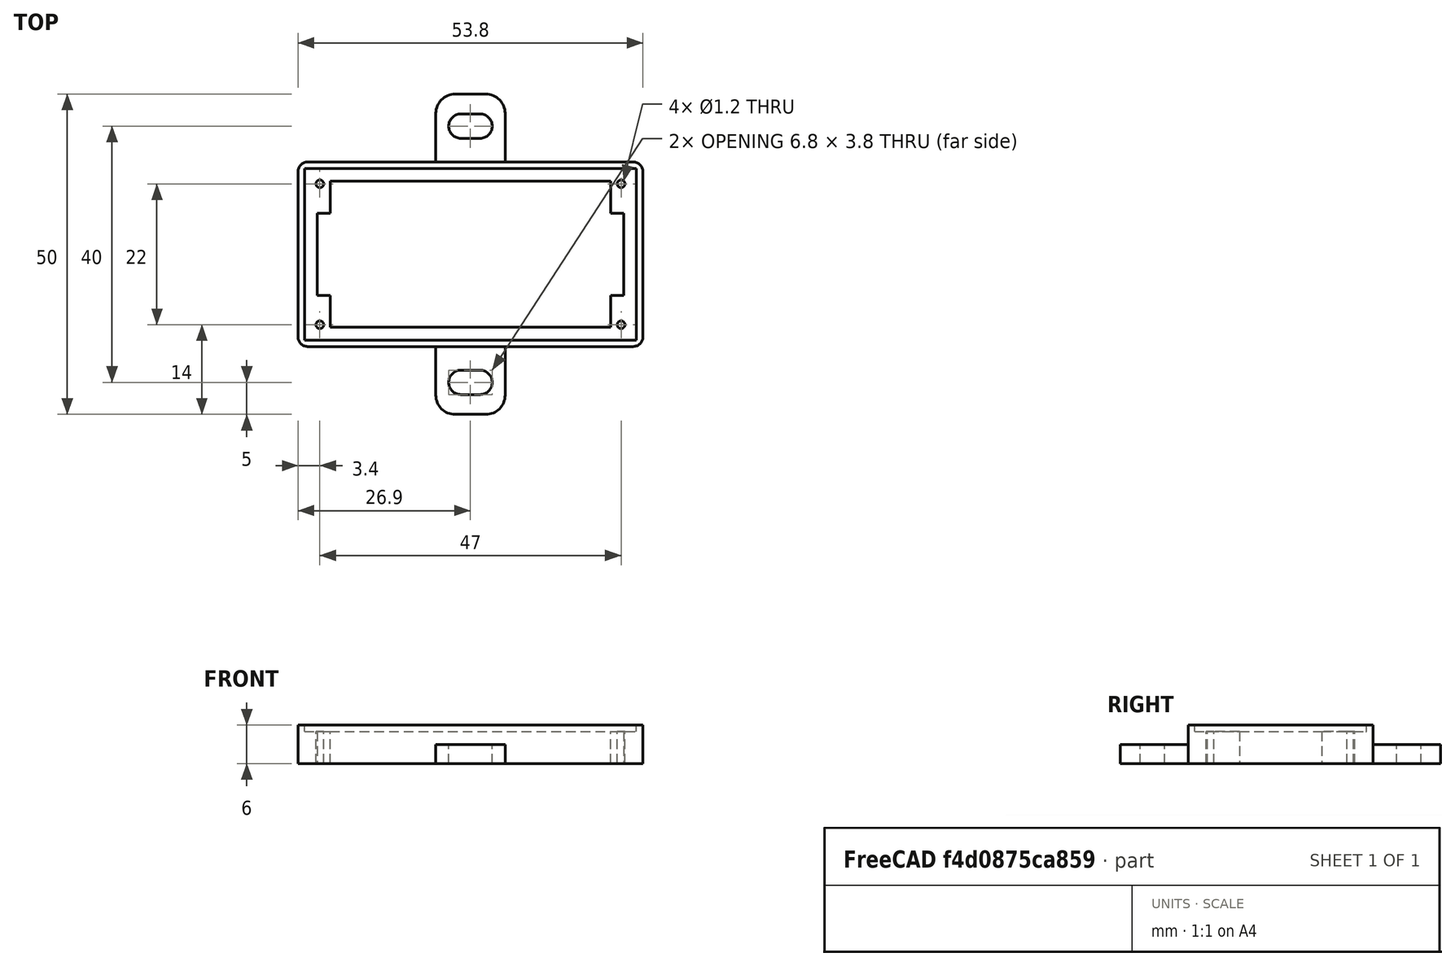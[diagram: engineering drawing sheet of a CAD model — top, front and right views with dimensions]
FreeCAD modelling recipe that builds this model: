
FCSTD DOCUMENT  (FreeCAD 0.18.4R)
Label: step_down_xl4015e1
License: All rights reserved
LicenseURL: http://en.wikipedia.org/wiki/All_rights_reserved
objects: Part::Box×4, Part::MultiFuse×3, Part::FeaturePython×2, Part::Cut×2, Spreadsheet::Sheet×1, Part::Cylinder×1, Part::Fillet×1, Part::Feature×1, App::Part×1
note: 14 computed .brp shape members not serialized (recipe doc carries the construction recipe); baked Part::Feature solids carry a one-line shape summary decoded from their .brp

FEATURE [Spreadsheet::Sheet] Spreadsheet  label="p"
  cells = A1=hole_x_dist; B1(hole_x_dist)=47; A2=hole_y_dist; B2(hole_y_dist)=22; A3=pcb_under; B3(pcb_under)=1.5; A4=pcb_x; B4(pcb_x)=51.8; A5=pcb_y; B5(pcb_y)=26.8; A6=hole_stand_x; B6(hole_stand_x)=4; A7=hole_stand_y; B7(hole_stand_y)=7; A8=hole_r; B8(hole_r)=0.6; A9=box_wall; B9(box_wall)=1; A10=under_layer; B10(under_layer)=3; A11=pcb_height; B11(pcb_height)=1.5
FEATURE [Part::Box] Box  label="bottom cube"
  AttacherType = Attacher::AttachEngine3D
  Height = 6
  Length = 53.8
  Width = 28.8
  expr: Width = p.pcb_y + p.box_wall * 2
  expr: Length = p.pcb_x + p.box_wall * 2
  expr: Height = p.pcb_under + p.pcb_height + p.under_layer
FEATURE [Part::Box] Box001  label="bottom extraction"
  AttacherType = Attacher::AttachEngine3D
  Height = 10
  Length = 47.8
  Placement = pos=(3,3,0) rot=(0,0,1;0rad)
  Width = 22.8
  expr: Placement.Base.y = p.under_pcb_border + p.box_wall
  expr: Placement.Base.x = p.under_pcb_border + p.box_wall
  expr: Length = p.pcb_x - p.under_pcb_border * 2
  expr: Width = p.pcb_y - p.under_pcb_border * 2
FEATURE [Part::Box] Box002  label="pcb extraction"
  AttacherType = Attacher::AttachEngine3D
  Height = 10
  Length = 51.8
  Placement = pos=(1,1,5) rot=(0,0,1;0rad)
  Width = 26.8
  expr: Placement.Base.z = p.under_pcb_border + p.under_layer
  expr: Placement.Base.y = p.box_wall
  expr: Placement.Base.x = p.box_wall
  expr: Length = p.pcb_x
  expr: Width = p.pcb_y
FEATURE [Part::MultiFuse] Fusion  label="bottom extraction001"
  Shapes = -> [Box001,Box002]
FEATURE [Part::Box] Box003  label="hole stand cube"
  AttacherType = Attacher::AttachEngine3D
  Height = 5
  Length = 4
  Placement = pos=(1,1,0) rot=(0,0,1;0rad)
  Width = 7
  expr: Placement.Base.y = p.box_wall
  expr: Placement.Base.x = p.box_wall
  expr: Height = p.under_layer + p.under_pcb_border
  expr: Width = p.hole_stand_y
  expr: Length = p.hole_stand_x
FEATURE [Part::FeaturePython] Array  label="hole stand array"  # Draft array (typed FeaturePython)
  Angle = 360
  ArrayType = 0
  Axis = (0,0,1)
  Base = -> Box003
  Center = (0,0,0)
  Fuse = false
  IntervalAxis = (0,0,0)
  IntervalX = (47.8,0,0)
  IntervalY = (0,19.8,0)
  IntervalZ = (0,0,1)
  NumberPolar = 1
  NumberX = 2
  NumberY = 2
  NumberZ = 1
  expr: IntervalY.y = p.pcb_y - p.hole_stand_y
  expr: IntervalX.x = p.pcb_x - p.hole_stand_x
FEATURE [Part::Cylinder] Cylinder  label="pcb hole"
  Angle = 360
  AttacherType = Attacher::AttachEngine3D
  Height = 10
  Placement = pos=(3.4,3.4,0) rot=(0,0,1;0rad)
  Radius = 0.6
  expr: Placement.Base.y = (p.box_wall * 2 + p.pcb_y - p.hole_y_dist) / 2
  expr: Placement.Base.x = (p.box_wall * 2 + p.pcb_x - p.hole_x_dist) / 2
  expr: Radius = p.hole_r
FEATURE [Part::FeaturePython] Array001  label="hole array"  # Draft array (typed FeaturePython)
  Angle = 360
  ArrayType = 0
  Axis = (0,0,1)
  Base = -> Cylinder
  Center = (0,0,0)
  Fuse = false
  IntervalAxis = (0,0,0)
  IntervalX = (47,0,0)
  IntervalY = (0,22,0)
  IntervalZ = (0,0,1)
  NumberPolar = 1
  NumberX = 2
  NumberY = 2
  NumberZ = 1
  expr: IntervalY.y = p.hole_y_dist
  expr: IntervalX.x = p.hole_x_dist
FEATURE [Part::Fillet] Fillet001  label="bottom cube fillet"
  Base = -> Box
  Edges = 4 edges r=1.5: [Edge1,Edge3,Edge5,Edge7]
FEATURE [Part::Feature] Cut002001  label="attach plane y dir001"
  shape: bbox 10.8 x 50 x 3 mm, 18 faces (baked)
FEATURE [Part::MultiFuse] Fusion002  label="bottom fusion"
  Shapes = -> [Fillet001,Cut002001]
FEATURE [Part::Cut] Cut  label="pcb box cut"
  Base = -> Fusion002
  Tool = -> Fusion
FEATURE [Part::MultiFuse] Fusion001  label="frame fusion"
  Shapes = -> [Array,Cut]
FEATURE [Part::Cut] Cut001  label="frame fusion with holes"
  Base = -> Fusion001
  Tool = -> Array001
FEATURE [App::Part] Part  label="pcb with 4 holes part"
  Group = -> [Fusion,Fusion002,Box002,Box003,Box001,Array001,Box,Cut,Array,Cylinder,Fusion001,Cut001]
  Origin = -> Origin
